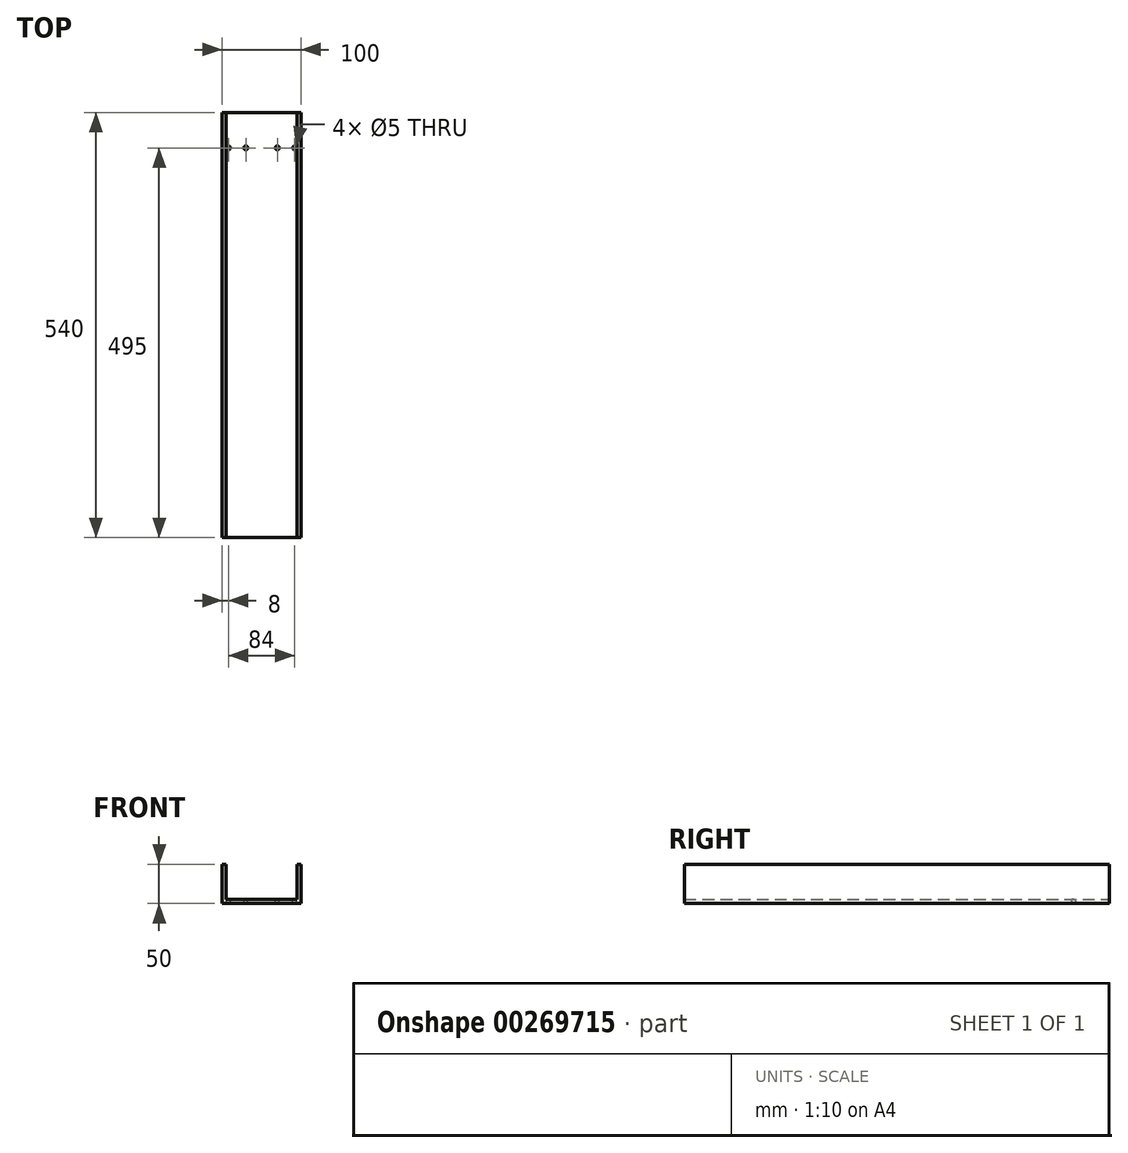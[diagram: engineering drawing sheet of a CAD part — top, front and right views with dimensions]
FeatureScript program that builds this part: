
annotation { "Feature Type Name" : "Feature", "Feature Type Description" : "" }
export const myFeature = defineFeature(function(context is Context, id is Id, definition is map)
    precondition{}
    {
        {
            var Q0;
            Q0=qCreatedBy(makeId("Front.planeOp"),FACE);
            var sketch = newSketch(context, id + "F0", { "sketchPlane" : qUnion([Q0])});
            skLineSegment(sketch, "E0", {"start": v(-50, 0) * mm, "end": v(50, 0) * mm});
            skLineSegment(sketch, "E1", {"start": v(50, 0) * mm, "end": v(50, 50) * mm});
            skLineSegment(sketch, "E2", {"start": v(50, 50) * mm, "end": v(45, 50) * mm});
            skLineSegment(sketch, "E3", {"start": v(45, 50) * mm, "end": v(45, 5) * mm});
            skLineSegment(sketch, "E4", {"start": v(45, 5) * mm, "end": v(-45, 5) * mm});
            skLineSegment(sketch, "E5", {"start": v(-45, 5) * mm, "end": v(-45, 50) * mm});
            skLineSegment(sketch, "E6", {"start": v(-45, 50) * mm, "end": v(-50, 50) * mm});
            skLineSegment(sketch, "E7", {"start": v(-50, 50) * mm, "end": v(-50, 0) * mm});
            skSolve(sketch);
        }
        {
            var Q0;
            Q0=makeQuery(id+"F0.imprint","IMPRINT",FACE,{"disambiguationData":[TD([[makeQuery(id+"F0.imprint","IMPRINT",EDGE,{"derivedFrom":sQuery(id+"F0.wireOp",EDGE,"E0")}),1.0]])]});
            extrude(context, id + "F1", {"entities" : qUnion([Q0]), "depth" : 540 * mm});
        }
        {
            var Q0;
            Q0=makeQuery(id+"F1.opExtrude","SWEPT_FACE",FACE,{"disambiguationData":[OSD([sQuery(id+"F0.wireOp",EDGE,"E0")])]});
            var sketch = newSketch(context, id + "F2", { "sketchPlane" : qUnion([Q0])});
            skLineSegment(sketch, "E8", {"start": v(-42, -38.78) * mm, "end": v(-42, 603.06) * mm, "construction": true});
            skLineSegment(sketch, "E9", {"start": v(42, 602.28) * mm, "end": v(42, -50.5) * mm, "construction": true});
            skLineSegment(sketch, "E10", {"start": v(0, 556.94) * mm, "end": v(0, -66.14) * mm, "construction": true});
            skPoint(sketch, "E10.startSnap0", {"position": v(0, 540) * mm});
            skLineSegment(sketch, "E11", {"start": v(-42, 45) * mm, "end": v(42, 45) * mm, "construction": true});
            skPoint(sketch, "E12", {"position": v(-42, 45) * mm});
            skPoint(sketch, "E13", {"position": v(42, 45) * mm});
            skLineSegment(sketch, "E14", {"start": v(-20, 45) * mm, "end": v(-20, 559.4) * mm, "construction": true});
            skLineSegment(sketch, "E15", {"start": v(20, 45) * mm, "end": v(20, 561.54) * mm, "construction": true});
            skPoint(sketch, "E16", {"position": v(-20, 45) * mm});
            skPoint(sketch, "E17", {"position": v(20, 45) * mm});
            skSolve(sketch);
        }
        {
            var Q0;
            Q0=sQuery(id+"F2.wireOp",VERTEX,"E12");
            var Q1;
            Q1=sQuery(id+"F2.wireOp",VERTEX,"E13");
            var Q2;
            Q2=sQuery(id+"F2.wireOp",VERTEX,"E16");
            var Q3;
            Q3=sQuery(id+"F2.wireOp",VERTEX,"E17");
            var Q4;
            Q4=makeQuery(id+"F1.opExtrude","SWEPT_BODY",BODY,{"disambiguationData":[OSD([sQuery(id+"F0.wireOp",EDGE,"E0"),sQuery(id+"F0.wireOp",EDGE,"E1"),sQuery(id+"F0.wireOp",EDGE,"E2"),sQuery(id+"F0.wireOp",EDGE,"E3"),sQuery(id+"F0.wireOp",EDGE,"E4"),sQuery(id+"F0.wireOp",EDGE,"E5"),sQuery(id+"F0.wireOp",EDGE,"E6"),sQuery(id+"F0.wireOp",EDGE,"E7")])]});
            hole(context, id + "F3", {"style" : HoleStyle.SIMPLE, "endStyle" : HoleEndStyle.THROUGH, "holeDiameter" : 5 * mm, "locations" : qUnion([Q0, Q1, Q2, Q3]), "scope" : qUnion([Q4]), "isTappedThrough" : true, "startStyle" : HoleStartStyle.PART});
        }
    });
